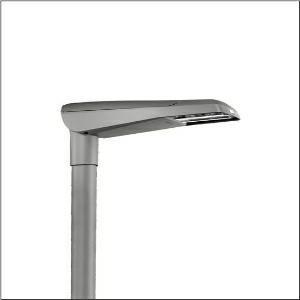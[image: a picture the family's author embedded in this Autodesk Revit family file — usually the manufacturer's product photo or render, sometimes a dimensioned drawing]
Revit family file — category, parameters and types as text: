
# Revit family: streetlight_sl_11_iq_micro___st0_5a_5xc1b51e08ce_0c76
name_source: partatom
category: Lighting Fixtures
units: mm (PartAtom-declared; Revit-internal decimal feet)

## family parameters
Cut with Voids When Loaded = No
Host = Face
Light Source = No
Part Type = Normal
Room Calculation Point = No
Round Connector Dimension = Use Diameter
Shared = No

## types (1)
- --- (1 x LED, 1860 lm, 12.6 W, 3000K)
    Apparent Load = 13 VA
    CIE Flux Codes = 42 72 97 100 100
    Color Rendering = 70
    Color Temperature = 3000K
    Default Elevation = 1800 mm
    Description = Streetlight SL 11 iQ micro, mast luminaire, primary light control with 3 zone facetted reflector, of plastic, silver coated, highly specular, primary optical cover: cover, of PMMA, transparent, light distribution: ST0.5a, light emission: direct distribution, primary light characteristic: asymmetric, installation type: post-top, side-entry, lamps: LED, High Power LED, rated values: 1.860lm | 12,6W | 147,6lm/W (begin service life); end service life: 1.860lm | 12,9W; at 50% lumin. flux: 930lm | 6,8W | 136,8lm/W, colour temperature: 3000K, colour rendering: CRI > 70, light colour: 730, light setting 1 begin service life: 100% | 1.860lm | 12,6W | 147,6lm/W | 3.000K, light setting 1 end service life: 12,9W, further light settings possible, control: optimised constant luminous flux control (CLO 2.0), Desk-Remote (wireless, voltage-free reading and setting of iQ features in the workshop via application-optimized NFC function/RFID function), Light-Fading, Smart-Wire, Night-Set, Lumen-Switch, Temp-Guard, Auto-Match, with cable H07RN-F 3x 1.5mm², mains connection: 230..240V, AC, 50/60Hz, connection cable pre-assembled, cable length: 5,5m, luminaire housing, of diecast aluminium, powder-coated, SITECO metallic grey (DB 702S), please order mast flange separately, inclination adjustable without tools: 0°, 5°, 10°, 15° (post-top) | 0°, -5°, -10°, -15° (side-entry), sealing non-destructively replaceable, multi-level sealing system, length: 600mm, width: 174mm, height: 116mm, mast flange for spigot size: 42mm (side-entry): 5XC10008XM4, 60/48mm (side-entry/post-top): 5XC10108XM2, 76/60mm (side-entry/post-top): 5XC10108XM1, equipment: standard, protection rating (complete): IP66, insulation class (complete): insulation class II (safety insulation), certification: CE, ENEC, ENEC+, VDE, impact resistance: IK10, permissible operating ambient temperature for outdoor applications: -25..+50°C, standard-compliant lighting for roads and squares, Environmental Product Declaration (EPD) tested and certified by an independent institute, packaging unit: 1 piece

Light Distribution: ST0.5a
    Height = 116 mm
    Lamp = 1 x LED
    Lamp Light Flux = 1860 lm
    Lamp Power = 12.6 W
    Lamp count = 1
    Length = 600 mm
    Luminous efficacy = 148 lm/W
    Manufacturer = Siteco
    ModVariant = No
    Model = 5XC1B51E08CE
    Number of Poles = 1
    OnlyDefault = Yes
    Power Factor = 1
    Product Name = Streetlight SL 11 iQ micro | ST0.5a
    Product group = mast luminaire | pylon top
    ProductGroupID = 6100
    Protection Class = Protection class II
    Protection Degree = IP 66
    RLX_Detail_Level = 1
    RLX_Emergency_Light_Flux = 0 lm
    RLX_Emergency_Type = 0
    RLX_Emergency_Type_DB = No
    RlxData = <blob elided: 26841 chars, md5=dc0c28ee>
    Socket = socket
    Standby Power = 0 W
    System Light Flux = 1860 lm
    System Power = 13 W
    Type Comments = factory setting: luminous flux: 100 % | dim-lin: 254 | 229 mA
    Type Image = l_1006566.jpg
    URL = http://relux.com
    VarID = @adj_021785
    Voltage = 0 V
    Weight = 0.00 kg
    Width = 174 mm

## geometry (parser evidence)
native form markers: Blend x4, Sweep x13
no freeform markers — native parametric forms only
